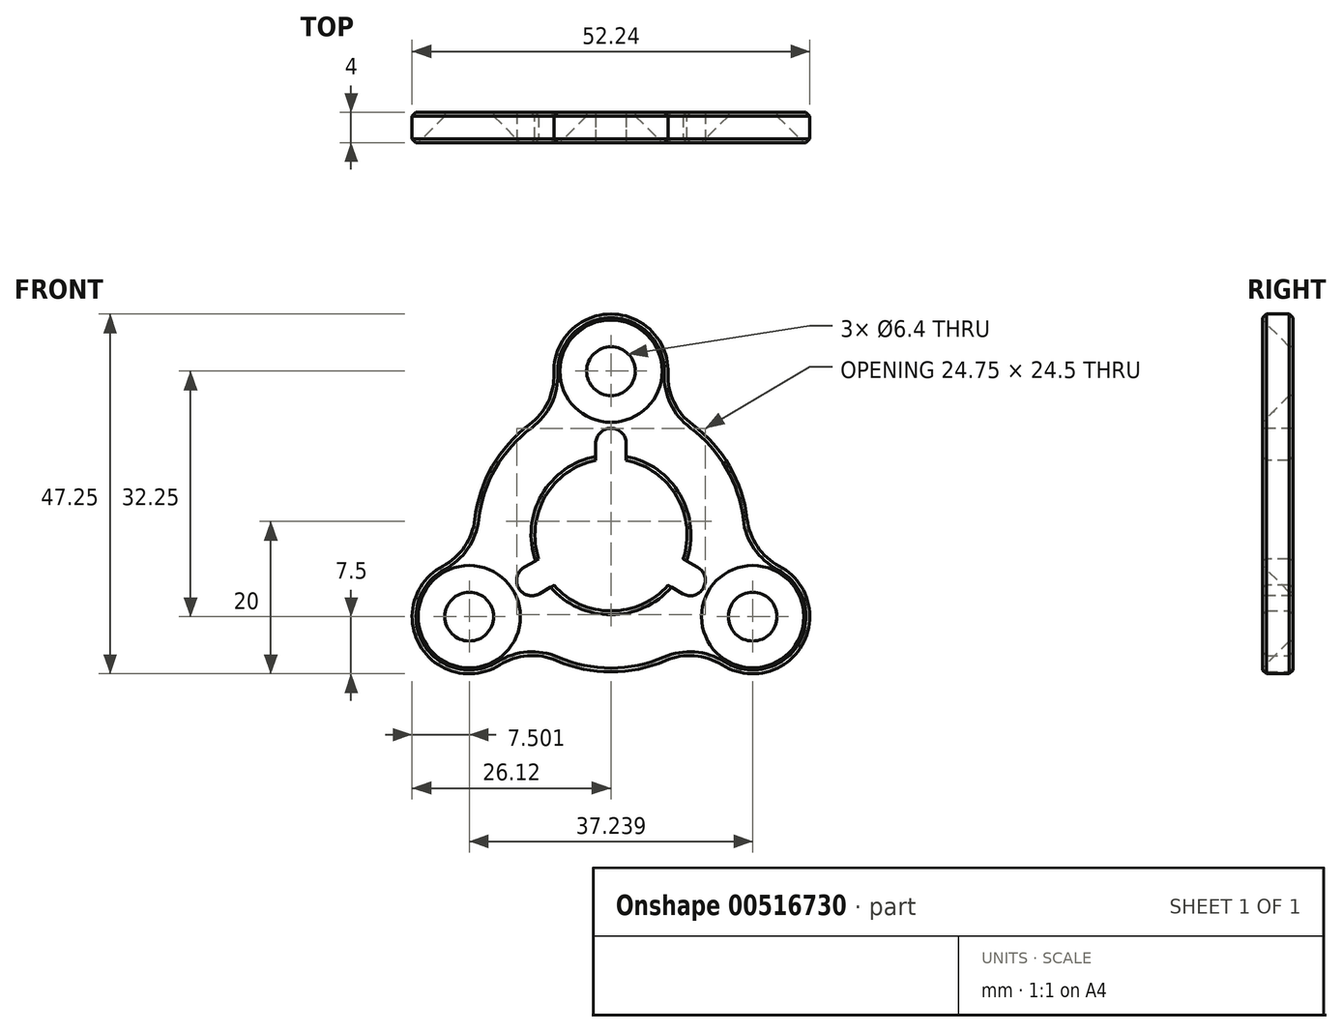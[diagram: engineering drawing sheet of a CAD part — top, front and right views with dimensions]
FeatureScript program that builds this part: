
annotation { "Feature Type Name" : "Feature", "Feature Type Description" : "" }
export const myFeature = defineFeature(function(context is Context, id is Id, definition is map)
    precondition{}
    {
        {
            var Q0;
            Q0=qCreatedBy(makeId("Front.planeOp"),FACE);
            var sketch = newSketch(context, id + "F0", { "sketchPlane" : qUnion([Q0])});
            skArc(sketch, "E0", {"start": v(-25.11, 14.5) * mm, "mid": v(-29, 0) * mm, "end": v(-25.11, -14.5) * mm, "construction": true});
            skLineSegment(sketch, "E1", {"start": v(0, 0) * mm, "end": v(0, -29) * mm, "construction": true});
            skLineSegment(sketch, "E2", {"start": v(-25.11, 14.5) * mm, "end": v(0, 0) * mm, "construction": true});
            skLineSegment(sketch, "E3", {"start": v(25.11, 14.5) * mm, "end": v(0, 0) * mm, "construction": true});
            skLineSegment(sketch, "E4.MirrorCS", {"start": v(-25.11, -14.5) * mm, "end": v(0, 0) * mm, "construction": true});
            skLineSegment(sketch, "E5.MirrorCS", {"start": v(25.11, -14.5) * mm, "end": v(0, 0) * mm, "construction": true});
            skCircle(sketch, "E6", {"center": v(0, 0) * mm, "radius": 21.5 * mm, "construction": true});
            skArc(sketch, "E7", {"start": v(7.5, 21.2) * mm, "mid": v(0, 29) * mm, "end": v(-7.5, 21.2) * mm});
            skArc(sketch, "E8", {"start": v(14.61, -17.1) * mm, "mid": v(25.11, -14.5) * mm, "end": v(22.1, -4.11) * mm});
            skArc(sketch, "E9", {"start": v(-22.1, -4.11) * mm, "mid": v(-25.11, -14.5) * mm, "end": v(-14.61, -17.1) * mm});
            skArc(sketch, "E10", {"start": v(-10.72, 14.46) * mm, "mid": v(-15.59, 9) * mm, "end": v(-17.88, 2.06) * mm});
            skArc(sketch, "E11.trimOffspring", {"start": v(0, -29) * mm, "mid": v(14.5, -25.11) * mm, "end": v(25.11, -14.5) * mm, "construction": true});
            skArc(sketch, "E12.trimOffspring", {"start": v(-7.16, -16.51) * mm, "mid": v(0, -18) * mm, "end": v(7.16, -16.51) * mm});
            skArc(sketch, "E13.trimOffspring", {"start": v(17.88, 2.06) * mm, "mid": v(15.59, 9) * mm, "end": v(10.72, 14.46) * mm});
            skArc(sketch, "E14.trimOffspring", {"start": v(25.11, 14.5) * mm, "mid": v(14.5, 25.11) * mm, "end": v(0, 29) * mm, "construction": true});
            skPoint(sketch, "E15.visualSharp", {"position": v(-5.98, 16.98) * mm});
            skArc(sketch, "E15.filletArc", {"start": v(-10.72, 14.46) * mm, "mid": v(-8.27, 17.43) * mm, "end": v(-7.5, 21.2) * mm});
            skPoint(sketch, "E16.visualSharp", {"position": v(-17.7, -3.3) * mm});
            skArc(sketch, "E16.filletArc", {"start": v(-22.1, -4.11) * mm, "mid": v(-19.23, -1.55) * mm, "end": v(-17.88, 2.06) * mm});
            skPoint(sketch, "E17.visualSharp", {"position": v(-11.71, -13.67) * mm});
            skArc(sketch, "E17.filletArc", {"start": v(-7.16, -16.51) * mm, "mid": v(-10.96, -15.88) * mm, "end": v(-14.61, -17.1) * mm});
            skPoint(sketch, "E18.visualSharp", {"position": v(11.71, -13.67) * mm});
            skArc(sketch, "E18.filletArc", {"start": v(14.61, -17.1) * mm, "mid": v(10.96, -15.88) * mm, "end": v(7.16, -16.51) * mm});
            skPoint(sketch, "E19.visualSharp", {"position": v(17.7, -3.3) * mm});
            skArc(sketch, "E19.filletArc", {"start": v(17.88, 2.06) * mm, "mid": v(19.23, -1.55) * mm, "end": v(22.1, -4.11) * mm});
            skPoint(sketch, "E20.visualSharp", {"position": v(5.98, 16.98) * mm});
            skArc(sketch, "E20.filletArc", {"start": v(7.5, 21.2) * mm, "mid": v(8.27, 17.43) * mm, "end": v(10.72, 14.46) * mm});
            skCircle(sketch, "E21", {"center": v(0, 0) * mm, "radius": 10 * mm});
            skSolve(sketch);
        }
        {
            var Q0;
            Q0=qSketchRegion(id+"F0",true);
            extrude(context, id + "F1", {"entities" : qUnion([Q0]), "depth" : 2 * mm, "offsetDistance" : 25 * mm, "hasSecondDirection" : true, "secondDirectionOppositeDirection" : true, "secondDirectionDepth" : 2 * mm});
        }
        {
            var Q0;
            Q0=makeQuery(id+"F1.opExtrude","CAP_EDGE",EDGE,{"disambiguationData":[OSD([sQuery(id+"F0.wireOp",EDGE,"TlV9cv7D-g5JN-84Zv-9bjP-qhInX7POgq7z")])],"isStart":false});
            var Q1;
            Q1=makeQuery(id+"F1.opExtrude","CAP_EDGE",EDGE,{"disambiguationData":[OSD([sQuery(id+"F0.wireOp",EDGE,"TlV9cv7D-g5JN-84Zv-9bjP-qhInX7POgq7z")])],"isStart":true});
            var Q2;
            Q2=makeQuery(id+"F1.opExtrude","CAP_EDGE",EDGE,{"disambiguationData":[OSD([sQuery(id+"F0.wireOp",EDGE,"E7")])],"isStart":false});
            var Q3;
            Q3=makeQuery(id+"F1.opExtrude","CAP_EDGE",EDGE,{"disambiguationData":[OSD([sQuery(id+"F0.wireOp",EDGE,"E7")])],"isStart":true});
            var Q4;
            Q4=makeQuery(id+"F1.opExtrude","CAP_EDGE",EDGE,{"disambiguationData":[OSD([sQuery(id+"F0.wireOp",EDGE,"E21")])],"isStart":false});
            var Q5;
            Q5=makeQuery(id+"F1.opExtrude","CAP_EDGE",EDGE,{"disambiguationData":[OSD([sQuery(id+"F0.wireOp",EDGE,"E21")])],"isStart":true});
            chamfer(context, id + "F2", {"entities" : qUnion([Q0, Q1, Q2, Q3, Q4, Q5]), "width" : .5 * mm, "tangentPropagation" : true});
        }
        {
            var Q0;
            Q0=makeQuery(id+"F1.opExtrude","CAP_FACE",FACE,{"disambiguationData":[OSD([sQuery(id+"F0.wireOp",EDGE,"E7"),sQuery(id+"F0.wireOp",EDGE,"E8"),sQuery(id+"F0.wireOp",EDGE,"E9"),sQuery(id+"F0.wireOp",EDGE,"E10"),sQuery(id+"F0.wireOp",EDGE,"E12.trimOffspring"),sQuery(id+"F0.wireOp",EDGE,"E13.trimOffspring"),sQuery(id+"F0.wireOp",EDGE,"E15.filletArc"),sQuery(id+"F0.wireOp",EDGE,"E16.filletArc"),sQuery(id+"F0.wireOp",EDGE,"E17.filletArc"),sQuery(id+"F0.wireOp",EDGE,"E18.filletArc"),sQuery(id+"F0.wireOp",EDGE,"E19.filletArc"),sQuery(id+"F0.wireOp",EDGE,"E20.filletArc"),sQuery(id+"F0.wireOp",EDGE,"E21")])],"isStart":false});
            var sketch = newSketch(context, id + "F3", { "sketchPlane" : qUnion([Q0])});
            skLineSegment(sketch, "E22", {"start": v(0, 28.5) * mm, "end": v(0, 0) * mm, "construction": true});
            skLineSegment(sketch, "E23", {"start": v(0, 0) * mm, "end": v(-24.68, -14.25) * mm, "construction": true});
            skLineSegment(sketch, "E24", {"start": v(24.68, -14.25) * mm, "end": v(0, 0) * mm, "construction": true});
            skPoint(sketch, "E25", {"position": v(18.62, -10.75) * mm});
            skPoint(sketch, "E26", {"position": v(0, 21.5) * mm});
            skPoint(sketch, "E27", {"position": v(-18.62, -10.75) * mm});
            skSolve(sketch);
        }
        {
            var Q0;
            Q0=sQuery(id+"F3.wireOp",VERTEX,"E26");
            var Q1;
            Q1=sQuery(id+"F3.wireOp",VERTEX,"E27");
            var Q2;
            Q2=sQuery(id+"F3.wireOp",VERTEX,"E25");
            var Q3;
            Q3=makeQuery(id+"F1.opExtrude","SWEPT_BODY",BODY,{"disambiguationData":[OSD([sQuery(id+"F0.wireOp",EDGE,"E7"),sQuery(id+"F0.wireOp",EDGE,"E8"),sQuery(id+"F0.wireOp",EDGE,"E9"),sQuery(id+"F0.wireOp",EDGE,"E10"),sQuery(id+"F0.wireOp",EDGE,"E12.trimOffspring"),sQuery(id+"F0.wireOp",EDGE,"E13.trimOffspring"),sQuery(id+"F0.wireOp",EDGE,"E15.filletArc"),sQuery(id+"F0.wireOp",EDGE,"E16.filletArc"),sQuery(id+"F0.wireOp",EDGE,"E17.filletArc"),sQuery(id+"F0.wireOp",EDGE,"E18.filletArc"),sQuery(id+"F0.wireOp",EDGE,"E19.filletArc"),sQuery(id+"F0.wireOp",EDGE,"E20.filletArc"),sQuery(id+"F0.wireOp",EDGE,"E21")])]});
            hole(context, id + "F4", {"style" : HoleStyle.C_SINK, "endStyle" : HoleEndStyle.THROUGH, "standardTappedOrClearance" : lookupTablePath({ "fit" : "Close", "standard" : "ISO", "size" : "M6", "type" : "Clearance" }), "standardBlindInLast" : lookupTablePath({ "fit" : "Close", "standard" : "ISO", "engagement" : "75%", "pitch" : "1 mm", "size" : "M6", "type" : "Clearance & tapped" }), "holeDiameter" : 6.4 * mm, "cSinkDiameter" : 13.44 * mm, "cSinkAngle" : 90 * degree, "majorDiameter" : 8 * mm, "isTappedThrough" : true, "tappedDepth" : 8 * mm, "tapClearance" : 3, "startFromSketch" : true, "locations" : qUnion([Q0, Q1, Q2]), "scope" : qUnion([Q3])});
        }
        {
            var Q0;
            Q0=makeQuery(id+"F1.opExtrude","CAP_FACE",FACE,{"disambiguationData":[OSD([sQuery(id+"F0.wireOp",EDGE,"E7"),sQuery(id+"F0.wireOp",EDGE,"E8"),sQuery(id+"F0.wireOp",EDGE,"E9"),sQuery(id+"F0.wireOp",EDGE,"E10"),sQuery(id+"F0.wireOp",EDGE,"E12.trimOffspring"),sQuery(id+"F0.wireOp",EDGE,"E13.trimOffspring"),sQuery(id+"F0.wireOp",EDGE,"E15.filletArc"),sQuery(id+"F0.wireOp",EDGE,"E16.filletArc"),sQuery(id+"F0.wireOp",EDGE,"E17.filletArc"),sQuery(id+"F0.wireOp",EDGE,"E18.filletArc"),sQuery(id+"F0.wireOp",EDGE,"E19.filletArc"),sQuery(id+"F0.wireOp",EDGE,"E20.filletArc"),sQuery(id+"F0.wireOp",EDGE,"E21")])],"isStart":false});
            var sketch = newSketch(context, id + "F5", { "sketchPlane" : qUnion([Q0])});
            skArc(sketch, "E28.0", {"start": v(2, 9.8) * mm, "mid": v(0, 10) * mm, "end": v(-2, 9.8) * mm});
            skLineSegment(sketch, "E29", {"start": v(-2, 9.8) * mm, "end": v(-2, 12) * mm});
            skLineSegment(sketch, "E30", {"start": v(2, 9.8) * mm, "end": v(2, 12) * mm});
            skArc(sketch, "E31", {"start": v(2, 12) * mm, "mid": v(0, 14) * mm, "end": v(-2, 12) * mm});
            skLineSegment(sketch, "E32", {"start": v(0, 0) * mm, "end": v(0, 28.5) * mm, "construction": true});
            skLineSegment(sketch, "E33.1.0", {"start": v(-7.49, -6.63) * mm, "end": v(-9.4, -7.73) * mm});
            skArc(sketch, "E33.1.1", {"start": v(-9.49, -3.17) * mm, "mid": v(-8.66, -5) * mm, "end": v(-7.49, -6.63) * mm});
            skLineSegment(sketch, "E33.1.2", {"start": v(-9.49, -3.17) * mm, "end": v(-11.4, -4.27) * mm});
            skArc(sketch, "E33.1.3", {"start": v(-11.4, -4.27) * mm, "mid": v(-12.12, -7) * mm, "end": v(-9.4, -7.73) * mm});
            skLineSegment(sketch, "E33.2.0", {"start": v(9.49, -3.17) * mm, "end": v(11.4, -4.27) * mm});
            skArc(sketch, "E33.2.1", {"start": v(7.49, -6.63) * mm, "mid": v(8.66, -5) * mm, "end": v(9.49, -3.17) * mm});
            skLineSegment(sketch, "E33.2.2", {"start": v(7.49, -6.63) * mm, "end": v(9.4, -7.73) * mm});
            skArc(sketch, "E33.2.3", {"start": v(9.4, -7.73) * mm, "mid": v(12.12, -7) * mm, "end": v(11.4, -4.27) * mm});
            skSolve(sketch);
        }
        {
            var Q0;
            Q0 = qSketchRegion(id + "F5", true);
            extrude(context, id + "F6", {"entities" : qUnion([Q0]), "operationType" : NewBodyOperationType.REMOVE, "endBound" : BoundingType.THROUGH_ALL, "oppositeDirection" : true, "depth" : 25 * mm, "offsetDistance" : 25 * mm});
        }
    });
